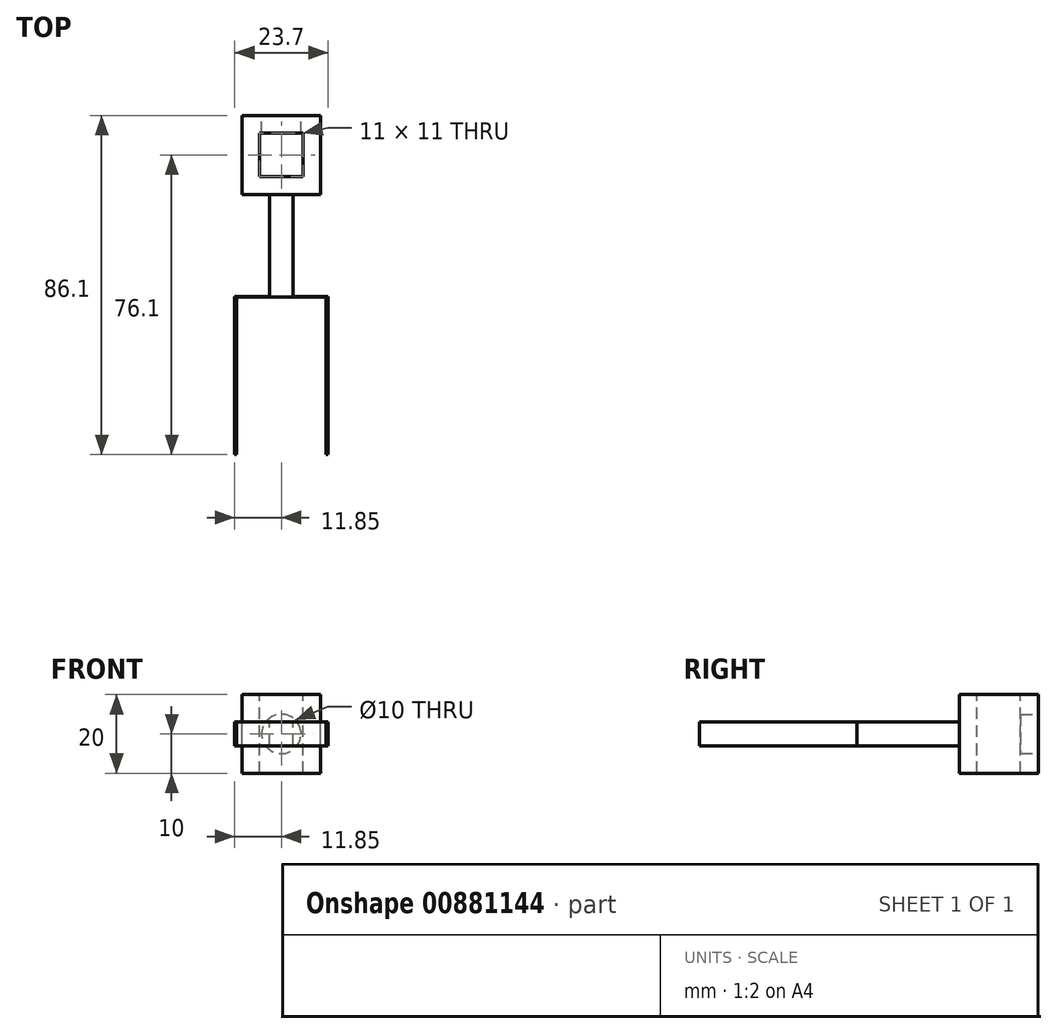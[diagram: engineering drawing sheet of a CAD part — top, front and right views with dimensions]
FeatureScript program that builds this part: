
annotation { "Feature Type Name" : "Feature", "Feature Type Description" : "" }
export const myFeature = defineFeature(function(context is Context, id is Id, definition is map)
    precondition{}
    {
        {
            var Q0;
            Q0=qCreatedBy(makeId("Front.planeOp"),FACE);
            var sketch = newSketch(context, id + "F0", { "sketchPlane" : qUnion([Q0])});
            skLineSegment(sketch, "E0.bottom", {"start": v(-10, -10) * mm, "end": v(10, -10) * mm});
            skLineSegment(sketch, "E0.top", {"start": v(-10, 10) * mm, "end": v(10, 10) * mm});
            skLineSegment(sketch, "E0.left", {"start": v(-10, -10) * mm, "end": v(-10, 10) * mm});
            skLineSegment(sketch, "E0.right", {"start": v(10, -10) * mm, "end": v(10, 10) * mm});
            skPoint(sketch, "E0.middle", {"position": v(0, 0) * mm});
            skSolve(sketch);
        }
        {
            var Q0;
            Q0=makeQuery(id+"F0.imprint","IMPRINT",FACE,{"disambiguationData":[TD([[makeQuery(id+"F0.imprint","IMPRINT",EDGE,{"derivedFrom":sQuery(id+"F0.wireOp",EDGE,"E0.bottom")}),1.0]])]});
            extrude(context, id + "F1", {"entities" : qUnion([Q0]), "depth" : 20 * mm, "offsetDistance" : 25 * mm});
        }
        {
            var Q0;
            Q0=makeQuery(id+"F1.opExtrude","SWEPT_FACE",FACE,{"disambiguationData":[OSD([sQuery(id+"F0.wireOp",EDGE,"E0.top")])]});
            var sketch = newSketch(context, id + "F2", { "sketchPlane" : qUnion([Q0])});
            skLineSegment(sketch, "E1.bottom", {"start": v(5.5, -15.5) * mm, "end": v(-5.5, -15.5) * mm});
            skLineSegment(sketch, "E1.top", {"start": v(5.5, -4.5) * mm, "end": v(-5.5, -4.5) * mm});
            skLineSegment(sketch, "E1.left", {"start": v(5.5, -15.5) * mm, "end": v(5.5, -4.5) * mm});
            skLineSegment(sketch, "E1.right", {"start": v(-5.5, -15.5) * mm, "end": v(-5.5, -4.5) * mm});
            skPoint(sketch, "E1.middle", {"position": v(0, -10) * mm});
            skPoint(sketch, "E1.middle.positionSnap0", {"position": v(-10, -10) * mm});
            skPoint(sketch, "E1.centerSnap0", {"position": v(-10, -10) * mm});
            skSolve(sketch);
        }
        {
            var Q0;
            Q0 = qSketchRegion(id + "F2", true);
            extrude(context, id + "F3", {"entities" : qUnion([Q0]), "operationType" : NewBodyOperationType.REMOVE, "oppositeDirection" : true, "depth" : 25 * mm, "offsetDistance" : 25 * mm});
        }
        {
            var Q0;
            Q0=makeQuery(id+"F1.opExtrude","CAP_FACE",FACE,{"disambiguationData":[OSD([sQuery(id+"F0.wireOp",EDGE,"E0.bottom"),sQuery(id+"F0.wireOp",EDGE,"E0.top"),sQuery(id+"F0.wireOp",EDGE,"E0.left"),sQuery(id+"F0.wireOp",EDGE,"E0.right")])],"isStart":false});
            var sketch = newSketch(context, id + "F4", { "sketchPlane" : qUnion([Q0])});
            skLineSegment(sketch, "E2.bottom", {"start": v(3, -3) * mm, "end": v(-3, -3) * mm});
            skLineSegment(sketch, "E2.top", {"start": v(3, 3) * mm, "end": v(-3, 3) * mm});
            skLineSegment(sketch, "E2.left", {"start": v(3, -3) * mm, "end": v(3, 3) * mm});
            skLineSegment(sketch, "E2.right", {"start": v(-3, -3) * mm, "end": v(-3, 3) * mm});
            skPoint(sketch, "E2.middle", {"position": v(0, 0) * mm});
            skSolve(sketch);
        }
        {
            var Q0;
            Q0 = qSketchRegion(id + "F4", true);
            extrude(context, id + "F5", {"entities" : qUnion([Q0]), "operationType" : NewBodyOperationType.ADD, "depth" : 26 * mm, "offsetDistance" : 25 * mm});
        }
        {
            var Q0;
            Q0=makeQuery(id+"F5.opExtrude","CAP_FACE",FACE,{"disambiguationData":[OSD([sQuery(id+"F4.wireOp",EDGE,"E2.bottom"),sQuery(id+"F4.wireOp",EDGE,"E2.top"),sQuery(id+"F4.wireOp",EDGE,"E2.left"),sQuery(id+"F4.wireOp",EDGE,"E2.right")])],"isStart":false});
            var sketch = newSketch(context, id + "F6", { "sketchPlane" : qUnion([Q0])});
            skLineSegment(sketch, "E3.bottom", {"start": v(11.85, -3) * mm, "end": v(-11.85, -3) * mm});
            skLineSegment(sketch, "E3.top", {"start": v(11.85, 3) * mm, "end": v(-11.85, 3) * mm});
            skLineSegment(sketch, "E3.left", {"start": v(11.85, -3) * mm, "end": v(11.85, 3) * mm});
            skLineSegment(sketch, "E3.right", {"start": v(-11.85, -3) * mm, "end": v(-11.85, 3) * mm});
            skPoint(sketch, "E3.middle", {"position": v(0, 0) * mm});
            skSolve(sketch);
        }
        {
            var Q0;
            Q0 = qSketchRegion(id + "F6", true);
            extrude(context, id + "F7", {"entities" : qUnion([Q0]), "operationType" : NewBodyOperationType.ADD, "depth" : 0.1 * mm, "offsetDistance" : 25 * mm});
        }
        {
            var Q0;
            Q0=makeQuery(id+"F7.opExtrude","CAP_FACE",FACE,{"disambiguationData":[OSD([sQuery(id+"F6.wireOp",EDGE,"E3.bottom"),sQuery(id+"F6.wireOp",EDGE,"E3.top"),sQuery(id+"F6.wireOp",EDGE,"E3.left"),sQuery(id+"F6.wireOp",EDGE,"E3.right")])],"isStart":false});
            var sketch = newSketch(context, id + "F8", { "sketchPlane" : qUnion([Q0])});
            skLineSegment(sketch, "E4.bottom", {"start": v(-11.85, 3) * mm, "end": v(-11.4, 3) * mm});
            skLineSegment(sketch, "E4.top", {"start": v(-11.85, -3) * mm, "end": v(-11.4, -3) * mm});
            skLineSegment(sketch, "E4.left", {"start": v(-11.85, 3) * mm, "end": v(-11.85, -3) * mm});
            skLineSegment(sketch, "E4.right", {"start": v(-11.4, 3) * mm, "end": v(-11.4, -3) * mm});
            skLineSegment(sketch, "E5.MirrorCS", {"start": v(11.85, -3) * mm, "end": v(11.4, -3) * mm});
            skLineSegment(sketch, "E6.MirrorCS", {"start": v(11.85, 3) * mm, "end": v(11.4, 3) * mm});
            skLineSegment(sketch, "E7.MirrorCS", {"start": v(11.4, 3) * mm, "end": v(11.4, -3) * mm});
            skLineSegment(sketch, "E8.MirrorCS", {"start": v(11.85, 3) * mm, "end": v(11.85, -3) * mm});
            skSolve(sketch);
        }
        {
            var Q0;
            Q0 = qSketchRegion(id + "F8", true);
            extrude(context, id + "F9", {"entities" : qUnion([Q0]), "operationType" : NewBodyOperationType.ADD, "depth" : 40 * mm, "offsetDistance" : 25 * mm});
        }
        {
            var Q0;
            Q0=makeQuery(id+"F1.opExtrude","CAP_FACE",FACE,{"disambiguationData":[OSD([sQuery(id+"F0.wireOp",EDGE,"E0.bottom"),sQuery(id+"F0.wireOp",EDGE,"E0.top"),sQuery(id+"F0.wireOp",EDGE,"E0.left"),sQuery(id+"F0.wireOp",EDGE,"E0.right")])],"isStart":true});
            var sketch = newSketch(context, id + "F10", { "sketchPlane" : qUnion([Q0])});
            skCircle(sketch, "E9", {"center": v(0, 0) * mm, "radius": 5 * mm});
            skSolve(sketch);
        }
        {
            var Q0;
            Q0 = qSketchRegion(id + "F10", true);
            extrude(context, id + "F11", {"entities" : qUnion([Q0]), "operationType" : NewBodyOperationType.REMOVE, "oppositeDirection" : true, "depth" : 10 * mm, "offsetDistance" : 25 * mm});
        }
    });
